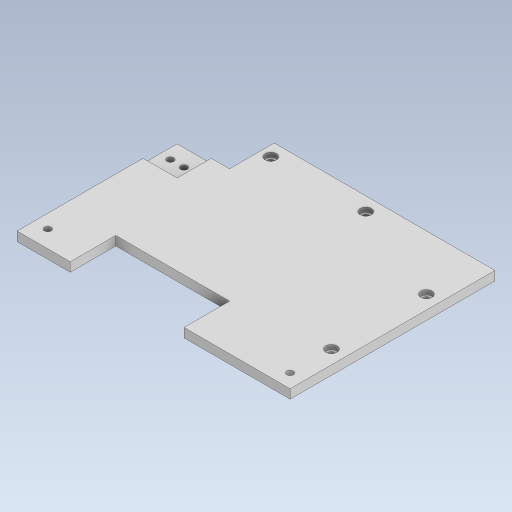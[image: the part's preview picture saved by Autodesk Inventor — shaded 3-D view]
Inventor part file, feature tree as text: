
AUTODESK INVENTOR PART (.ipt)
format: ipt  version: 2023.5 (Build 275446000, 446)  size: 362,496 bytes
history: native  units: in
note: dims shown in document units (in); Inventor stores cm internally (conversion verified against a paired STEP export)
features: extrude x2, sketch x1
ambient origin geometry x8: Origin, YZ Plane, XZ Plane, XY Plane, X Axis, Y Axis, Z Axis, Center Point
bodies: Body1 (feature_tree)
feature tree (3):
  sketch  "Sketch1"  dims[d0=4.7244in d1=3.5433in d21=0.1181in d22=0.2559in d23=0.1181in d24=0.2559in d25=0.1181in d27=0.1181in d32=0.1969in d38=0.1181in d39=0.1969in d40=0.2362in d41=0.1969in d42=0.1181in d43=0.2362in d44=0.2362in d45=0.1181in d46=0.2362in d59=0.7736in d60=0.1181in d61=0.1969in d63=0.2953in d64=0.1575in d65=0.0in d66=0.0787in d67=0.0in d68=0.1181in d69=0.1181in d70=0.8219in d71=0.8219in d72=0.1969in d73=0.1969in d74=0.0in d75=0.0in d76=0.2953in d77=0.2953in d78=0.2953in d79=0.2953in d81=0.315in d33=0.0197in d34=0.0344in d35=0.0197in d36=0.0344in]
  extrude  "Extrusion3"  Depth=3.5433in
  extrude  "Extrusion4"  Depth=0.315in
